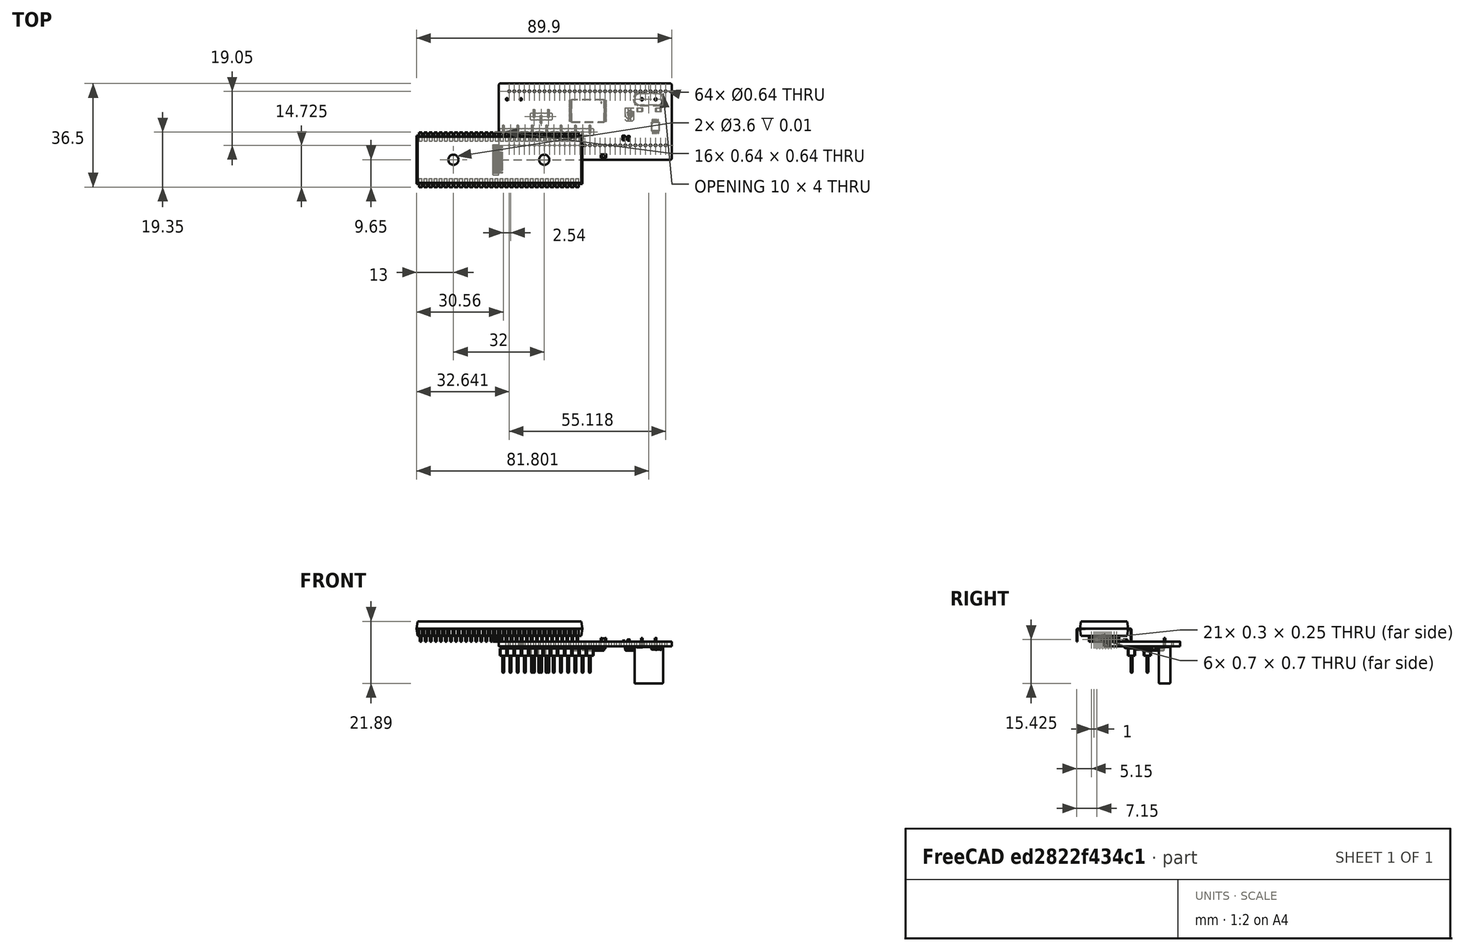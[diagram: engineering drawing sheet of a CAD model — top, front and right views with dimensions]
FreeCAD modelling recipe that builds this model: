
FCSTD DOCUMENT  (FreeCAD 0.19R24291 (Git))
Label: Ultra-MSX-VDP-pinstyle
License: All rights reserved
LicenseURL: http://en.wikipedia.org/wiki/All_rights_reserved
objects: Part::Feature×143, App::Link×51, App::Part×22, PartDesign::CoordinateSystem×1, Sketcher::SketchObject×1
note: 145 computed .brp shape members not serialized (recipe doc carries the construction recipe); baked Part::Feature solids carry a one-line shape summary decoded from their .brp

FEATURE [PartDesign::CoordinateSystem] Local_CS_a649
  AttacherType = Attacher::AttachEngine3D
FEATURE [Part::Feature] Pcb_a649
  Placement = pos=(-95.1,117.3,0) rot=(0,0,1;0rad)
  shape: bbox 60.9 x 26.85 x 1.6 mm, 78 faces (baked)
FEATURE [Sketcher::SketchObject] PCB_Sketch_a649
  FullyConstrained = false
  sketch-geometry (8):
    g0: LineSegment StartX=60.4 StartY=26.85 StartZ=0 EndX=0.5 EndY=26.85 EndZ=0
    g1: LineSegment StartX=4e-16 StartY=26.35 StartZ=0 EndX=1e-16 EndY=0.5 EndZ=0
    g2: LineSegment StartX=0.5 StartY=0 StartZ=0 EndX=60.4 EndY=-1.3e-15 EndZ=0
    g3: LineSegment StartX=60.9 StartY=0.5 StartZ=0 EndX=60.9 EndY=26.35 EndZ=0
    g4: ArcOfCircle CenterX=0.500001 CenterY=26.35 CenterZ=0 NormalX=0 NormalY=0 NormalZ=-1 AngleXU=2.66714e-06 Radius=0.500001 StartAngle=0 EndAngle=1.57079
    g5: ArcOfCircle CenterX=60.4 CenterY=0.500001 CenterZ=0 NormalX=0 NormalY=0 NormalZ=-1 AngleXU=-3.14159 Radius=0.500001 StartAngle=0 EndAngle=1.57079
    g6: ArcOfCircle CenterX=0.500001 CenterY=0.500001 CenterZ=0 NormalX=0 NormalY=0 NormalZ=-1 AngleXU=-1.57079 Radius=0.500001 StartAngle=0 EndAngle=1.57079
    g7: ArcOfCircle CenterX=60.4 CenterY=26.35 CenterZ=0 NormalX=0 NormalY=0 NormalZ=-1 AngleXU=1.5708 Radius=0.500001 StartAngle=0 EndAngle=1.57079
  constraints (8):
    c: Coincident(g1,g6)
    c: Coincident(g1,g4)
    c: Coincident(g2,g6)
    c: Coincident(g0,g4)
    c: Coincident(g2,g5)
    c: Coincident(g0,g7)
    c: Coincident(g3,g5)
    c: Coincident(g3,g7)
FEATURE [Part::Feature] Shape  label="C6_C_0603_1608Metric_e4ffc2d5bdca"
  Placement = pos=(45.7,7.5,0) rot=(0,0,1;1.5708rad)
  shape: bbox 0.8 x 1.6 x 0.8 mm, 28 faces (baked)
FEATURE [Part::Feature] Shape001  label="R82_R_0603_1608Metric_d4caecac030a"
  Placement = pos=(43.95,7.7,0) rot=(0,0,1;1.5708rad)
  shape: bbox 0.8 x 1.6 x 0.45 mm, 26 faces (baked)
FEATURE [App::Link] R82_R_0603_1608Metric_d4caecac030a_ln_  label="R81_R_0603_1608Metric_e3e91bc86c1a"
  LinkPlacement = pos=(47.2,7.9,0) rot=(0,0,1;1.5708rad)
  LinkedObject = -> Shape001
  Placement = pos=(47.2,7.9,0) rot=(0,0,1;1.5708rad)
FEATURE [App::Link] C6_C_0603_1608Metric_e4ffc2d5bdca_ln_  label="C16_C_0603_1608Metric_4bdb616e9b66"
  LinkPlacement = pos=(37.9,3.3,0) rot=(0,0,1;0rad)
  LinkedObject = -> Shape
  Placement = pos=(37.9,3.3,0) rot=(0,0,1;0rad)
FEATURE [App::Link] C6_C_0603_1608Metric_e4ffc2d5bdca_ln_001  label="C8_C_0603_1608Metric_43c608d33d12"
  LinkPlacement = pos=(42.475,7.3,0) rot=(0,0,1;1.5708rad)
  LinkedObject = -> Shape
  Placement = pos=(42.475,7.3,0) rot=(0,0,1;1.5708rad)
FEATURE [Part::Feature] Shape002  label="L3_L_0805_2012Metric_7024b431f41a"
  Placement = pos=(36.8375,1.3,0) rot=(0,0,1;0rad)
  shape: bbox 2 x 1.25 x 1.25 mm, 28 faces (baked)
FEATURE [App::Link] R82_R_0603_1608Metric_d4caecac030a_ln_001  label="R84_R_0603_1608Metric_7d963f7814c4"
  LinkPlacement = pos=(10.7,2.7,0) rot=(0,0,-1;1.5708rad)
  LinkedObject = -> Shape001
  Placement = pos=(10.7,2.7,0) rot=(0,0,-1;1.5708rad)
FEATURE [App::Link] R82_R_0603_1608Metric_d4caecac030a_ln_002  label="R83_R_0603_1608Metric_5f107b2ae899"
  LinkPlacement = pos=(38.475,6.9,0) rot=(0,0,1;3.14159rad)
  LinkedObject = -> Shape001
  Placement = pos=(38.475,6.9,0) rot=(0,0,1;3.14159rad)
FEATURE [App::Link] C6_C_0603_1608Metric_e4ffc2d5bdca_ln_002  label="C14_C_0603_1608Metric_0866816aecf6"
  LinkPlacement = pos=(15.3,25.7,0) rot=(0,0,1;3.14159rad)
  LinkedObject = -> Shape
  Placement = pos=(15.3,25.7,0) rot=(0,0,1;3.14159rad)
FEATURE [App::Link] R82_R_0603_1608Metric_d4caecac030a_ln_003  label="R60_R_0603_1608Metric_ee9b7d5e1906"
  LinkPlacement = pos=(23.9125,3.00625,0) rot=(0,0,1;0rad)
  LinkedObject = -> Shape001
  Placement = pos=(23.9125,3.00625,0) rot=(0,0,1;0rad)
FEATURE [App::Link] C6_C_0603_1608Metric_e4ffc2d5bdca_ln_003  label="C7_C_0603_1608Metric_cf974e6831ff"
  LinkPlacement = pos=(40.75,7.325,0) rot=(0,0,1;1.5708rad)
  LinkedObject = -> Shape
  Placement = pos=(40.75,7.325,0) rot=(0,0,1;1.5708rad)
FEATURE [App::Link] R82_R_0603_1608Metric_d4caecac030a_ln_004  label="R27_R_0603_1608Metric_a411e8e7a906"
  LinkPlacement = pos=(57.3,7.7,-1.6) rot=(0,1,0;3.14159rad)
  LinkedObject = -> Shape001
  Placement = pos=(57.3,7.7,-1.6) rot=(0,1,0;3.14159rad)
FEATURE [App::Link] R82_R_0603_1608Metric_d4caecac030a_ln_005  label="R14_R_0603_1608Metric_b666e58988c9"
  LinkPlacement = pos=(37.9,1.4,-1.6) rot=(0,1,0;3.14159rad)
  LinkedObject = -> Shape001
  Placement = pos=(37.9,1.4,-1.6) rot=(0,1,0;3.14159rad)
FEATURE [App::Link] R82_R_0603_1608Metric_d4caecac030a_ln_006  label="R53_R_0603_1608Metric_dd796e6052a9"
  LinkPlacement = pos=(16.5,7.3,-1.6) rot=(1,0,0;3.14159rad)
  LinkedObject = -> Shape001
  Placement = pos=(16.5,7.3,-1.6) rot=(1,0,0;3.14159rad)
FEATURE [App::Link] C6_C_0603_1608Metric_e4ffc2d5bdca_ln_005  label="C15_C_0603_1608Metric_af0c3dbdae54"
  LinkPlacement = pos=(57.7,11.7,-1.6) rot=(0.707107,-0.707107,0;3.14159rad)
  LinkedObject = -> Shape
  Placement = pos=(57.7,11.7,-1.6) rot=(0.707107,-0.707107,0;3.14159rad)
FEATURE [App::Link] R82_R_0603_1608Metric_d4caecac030a_ln_007  label="R21_R_0603_1608Metric_f35c04f488f9"
  LinkPlacement = pos=(50,8.2125,-1.6) rot=(0.707107,0.707107,0;3.14159rad)
  LinkedObject = -> Shape001
  Placement = pos=(50,8.2125,-1.6) rot=(0.707107,0.707107,0;3.14159rad)
FEATURE [Part::Feature] Shape003  label="R4_R_0805_2012Metric_f107bcb44f6e"
  Placement = pos=(49.5875,17.65,-1.6) rot=(1,0,0;3.14159rad)
  shape: bbox 2 x 1.2 x 0.45 mm, 26 faces (baked)
FEATURE [App::Link] R82_R_0603_1608Metric_d4caecac030a_ln_008  label="R23_R_0603_1608Metric_cfb541b6819d"
  LinkPlacement = pos=(34.4,11.05,-1.6) rot=(0.707107,0.707107,0;3.14159rad)
  LinkedObject = -> Shape001
  Placement = pos=(34.4,11.05,-1.6) rot=(0.707107,0.707107,0;3.14159rad)
FEATURE [App::Link] R82_R_0603_1608Metric_d4caecac030a_ln_009  label="R15_R_0603_1608Metric_62d8d2cdaec6"
  LinkPlacement = pos=(43.9,1.7,-1.6) rot=(0.707107,-0.707107,0;3.14159rad)
  LinkedObject = -> Shape001
  Placement = pos=(43.9,1.7,-1.6) rot=(0.707107,-0.707107,0;3.14159rad)
FEATURE [Part::Feature] Shape004  label="U6_VSSOP_10_3x3mm_P05mm_53867965ed20"
  Placement = pos=(55.15,11.7,-1.6) rot=(0.707107,-0.707107,0;3.14159rad)
  shape: bbox 3 x 4.9 x 1.2 mm, 186 faces (baked)
FEATURE [App::Link] C6_C_0603_1608Metric_e4ffc2d5bdca_ln_006  label="C3_C_0603_1608Metric_be4dabc485b9"
  LinkPlacement = pos=(59.7,21.2,-1.6) rot=(0.707107,0.707107,0;3.14159rad)
  LinkedObject = -> Shape
  Placement = pos=(59.7,21.2,-1.6) rot=(0.707107,0.707107,0;3.14159rad)
FEATURE [App::Link] R82_R_0603_1608Metric_d4caecac030a_ln_010  label="R1_R_0603_1608Metric_ed6f3b55dae2"
  LinkPlacement = pos=(12.8,21.75,-1.6) rot=(0.382683,0.92388,0;3.14159rad)
  LinkedObject = -> Shape001
  Placement = pos=(12.8,21.75,-1.6) rot=(0.382683,0.92388,0;3.14159rad)
FEATURE [App::Link] R82_R_0603_1608Metric_d4caecac030a_ln_011  label="R49_R_0603_1608Metric_953d89943b0f"
  LinkPlacement = pos=(31.9,7.3,-1.6) rot=(1,0,0;3.14159rad)
  LinkedObject = -> Shape001
  Placement = pos=(31.9,7.3,-1.6) rot=(1,0,0;3.14159rad)
FEATURE [Part::Feature] Shape005  label="U14_TSOP_I_28_118x8mm_P055mm_c181658d2376"
  Placement = pos=(31.3,17.25,-1.6) rot=(0,1,0;3.14159rad)
  shape: bbox 13.2 x 8 x 1.6 mm, 456 faces (baked)
FEATURE [Part::Feature] Shape006  label="Y3_Crystal_HC49-U_Vertical_0fe1bbda450f"
  Placement = pos=(55.2409,21.3,-1.6) rot=(0,1,0;3.14159rad)
  shape: bbox 10.9 x 4.65 x 16 mm, 26 faces (baked)
FEATURE [App::Link] R4_R_0805_2012Metric_f107bcb44f6e_ln_  label="R2_R_0805_2012Metric_293fb1e13199"
  LinkPlacement = pos=(6.3,17.6,-1.6) rot=(1,0,0;3.14159rad)
  LinkedObject = -> Shape003
  Placement = pos=(6.3,17.6,-1.6) rot=(1,0,0;3.14159rad)
FEATURE [App::Link] R82_R_0603_1608Metric_d4caecac030a_ln_012  label="R5_R_0603_1608Metric_b329b1c24be4"
  LinkPlacement = pos=(16.8166,21.9834,-1.6) rot=(0.382683,0.92388,0;3.14159rad)
  LinkedObject = -> Shape001
  Placement = pos=(16.8166,21.9834,-1.6) rot=(0.382683,0.92388,0;3.14159rad)
FEATURE [Part::Feature] Shape007  label="C5_Sprague_Goodman_SGC3_37e8c659f2e6"
  Placement = pos=(46.025,15.9,-1.6) rot=(0.707107,0.707107,0;3.14159rad)
  shape: bbox 3.247 x 4.625 x 1.5 mm, 36 faces (baked)
FEATURE [App::Link] R82_R_0603_1608Metric_d4caecac030a_ln_013  label="R61_R_0603_1608Metric_2d9e7edbb70d"
  LinkPlacement = pos=(58.75,9.175,-1.6) rot=(0,1,0;3.14159rad)
  LinkedObject = -> Shape001
  Placement = pos=(58.75,9.175,-1.6) rot=(0,1,0;3.14159rad)
FEATURE [App::Link] R82_R_0603_1608Metric_d4caecac030a_ln_014  label="R7_R_0603_1608Metric_b15c88e18e3f"
  LinkPlacement = pos=(23.1,22.1,-1.6) rot=(1,0,0;3.14159rad)
  LinkedObject = -> Shape001
  Placement = pos=(23.1,22.1,-1.6) rot=(1,0,0;3.14159rad)
FEATURE [App::Link] R82_R_0603_1608Metric_d4caecac030a_ln_015  label="R54_R_0603_1608Metric_722876daf014"
  LinkPlacement = pos=(21.55,7.3,-1.6) rot=(0,1,0;3.14159rad)
  LinkedObject = -> Shape001
  Placement = pos=(21.55,7.3,-1.6) rot=(0,1,0;3.14159rad)
FEATURE [App::Link] R82_R_0603_1608Metric_d4caecac030a_ln_016  label="R6_R_0603_1608Metric_8a82445061e6"
  LinkPlacement = pos=(31.45,22.35,-1.6) rot=(0,1,0;3.14159rad)
  LinkedObject = -> Shape001
  Placement = pos=(31.45,22.35,-1.6) rot=(0,1,0;3.14159rad)
FEATURE [App::Link] C5_Sprague_Goodman_SGC3_37e8c659f2e6_ln_  label="C1_Sprague_Goodman_SGC3_dd31bb1523f4"
  LinkPlacement = pos=(4.5,14.75,-1.6) rot=(1,0,0;3.14159rad)
  LinkedObject = -> Shape007
  Placement = pos=(4.5,14.75,-1.6) rot=(1,0,0;3.14159rad)
FEATURE [App::Link] C6_C_0603_1608Metric_e4ffc2d5bdca_ln_007  label="C2_C_0603_1608Metric_0b1b18837ebd"
  LinkPlacement = pos=(3.1,17.8,-1.6) rot=(1,0,0;3.14159rad)
  LinkedObject = -> Shape
  Placement = pos=(3.1,17.8,-1.6) rot=(1,0,0;3.14159rad)
FEATURE [App::Link] R82_R_0603_1608Metric_d4caecac030a_ln_017  label="R57_R_0603_1608Metric_aec65f8ff485"
  LinkPlacement = pos=(9.5,12.1,-1.6) rot=(0,1,0;3.14159rad)
  LinkedObject = -> Shape001
  Placement = pos=(9.5,12.1,-1.6) rot=(0,1,0;3.14159rad)
FEATURE [Part::Feature] Shape008  label="C73_C_0805_2012Metric_05153e2cdc69"
  Placement = pos=(56.2,17.5,-1.6) rot=(0,1,0;3.14159rad)
  shape: bbox 2 x 1.25 x 1.25 mm, 28 faces (baked)
FEATURE [App::Link] R82_R_0603_1608Metric_d4caecac030a_ln_018  label="R20_R_0603_1608Metric_7d7dade67ea7"
  LinkPlacement = pos=(24.3,12.1,-1.6) rot=(1,0,0;3.14159rad)
  LinkedObject = -> Shape001
  Placement = pos=(24.3,12.1,-1.6) rot=(1,0,0;3.14159rad)
FEATURE [App::Link] R82_R_0603_1608Metric_d4caecac030a_ln_019  label="R13_R_0603_1608Metric_307ab71b2f2b"
  LinkPlacement = pos=(41.65,1.65,-1.6) rot=(0,1,0;3.14159rad)
  LinkedObject = -> Shape001
  Placement = pos=(41.65,1.65,-1.6) rot=(0,1,0;3.14159rad)
FEATURE [App::Link] R82_R_0603_1608Metric_d4caecac030a_ln_020  label="R51_R_0603_1608Metric_7bd6d0df39b7"
  LinkPlacement = pos=(19.5,12.1,-1.6) rot=(1,0,0;3.14159rad)
  LinkedObject = -> Shape001
  Placement = pos=(19.5,12.1,-1.6) rot=(1,0,0;3.14159rad)
FEATURE [App::Link] R82_R_0603_1608Metric_d4caecac030a_ln_021  label="R22_R_0603_1608Metric_cb1c37444e2f"
  LinkPlacement = pos=(52.6,8.2125,-1.6) rot=(0.707107,0.707107,0;3.14159rad)
  LinkedObject = -> Shape001
  Placement = pos=(52.6,8.2125,-1.6) rot=(0.707107,0.707107,0;3.14159rad)
FEATURE [App::Link] C6_C_0603_1608Metric_e4ffc2d5bdca_ln_008  label="C12_C_0603_1608Metric_32ee04979fd2"
  LinkPlacement = pos=(52.55,11.925,-1.6) rot=(0.707107,0.707107,0;3.14159rad)
  LinkedObject = -> Shape
  Placement = pos=(52.55,11.925,-1.6) rot=(0.707107,0.707107,0;3.14159rad)
FEATURE [App::Link] C6_C_0603_1608Metric_e4ffc2d5bdca_ln_009  label="C10_C_0603_1608Metric_ed01532d6a4e"
  LinkPlacement = pos=(38.1,2.9,-1.6) rot=(1,0,0;3.14159rad)
  LinkedObject = -> Shape
  Placement = pos=(38.1,2.9,-1.6) rot=(1,0,0;3.14159rad)
FEATURE [App::Link] R82_R_0603_1608Metric_d4caecac030a_ln_022  label="R56_R_0603_1608Metric_1c0ae7ad8c6e"
  LinkPlacement = pos=(1.9,7.3,-1.6) rot=(0,1,0;3.14159rad)
  LinkedObject = -> Shape001
  Placement = pos=(1.9,7.3,-1.6) rot=(0,1,0;3.14159rad)
FEATURE [App::Link] R82_R_0603_1608Metric_d4caecac030a_ln_023  label="R50_R_0603_1608Metric_f5e2b95ccbbe"
  LinkPlacement = pos=(29.7,12.05,-1.6) rot=(0,1,0;3.14159rad)
  LinkedObject = -> Shape001
  Placement = pos=(29.7,12.05,-1.6) rot=(0,1,0;3.14159rad)
FEATURE [App::Link] C6_C_0603_1608Metric_e4ffc2d5bdca_ln_010  label="C17_C_0603_1608Metric_ba9556bdb5b0"
  LinkPlacement = pos=(54.95,15.7,-1.6) rot=(0,1,0;3.14159rad)
  LinkedObject = -> Shape
  Placement = pos=(54.95,15.7,-1.6) rot=(0,1,0;3.14159rad)
FEATURE [App::Link] R82_R_0603_1608Metric_d4caecac030a_ln_024  label="R25_R_0603_1608Metric_d3d0e9069176"
  LinkPlacement = pos=(34.35,7.95,-1.6) rot=(0.707107,0.707107,0;3.14159rad)
  LinkedObject = -> Shape001
  Placement = pos=(34.35,7.95,-1.6) rot=(0.707107,0.707107,0;3.14159rad)
FEATURE [App::Link] C6_C_0603_1608Metric_e4ffc2d5bdca_ln_011  label="C18_C_0603_1608Metric_0a9993050c82"
  LinkPlacement = pos=(57.7,14.9,-1.6) rot=(0.707107,-0.707107,0;3.14159rad)
  LinkedObject = -> Shape
  Placement = pos=(57.7,14.9,-1.6) rot=(0.707107,-0.707107,0;3.14159rad)
FEATURE [App::Link] R82_R_0603_1608Metric_d4caecac030a_ln_025  label="R52_R_0603_1608Metric_1314e578b8fa"
  LinkPlacement = pos=(26.9875,7.3,-1.6) rot=(1,0,0;3.14159rad)
  LinkedObject = -> Shape001
  Placement = pos=(26.9875,7.3,-1.6) rot=(1,0,0;3.14159rad)
FEATURE [App::Link] R82_R_0603_1608Metric_d4caecac030a_ln_026  label="R59_R_0603_1608Metric_51d35e5e8522"
  LinkPlacement = pos=(11.45,7.3,-1.6) rot=(1,0,0;3.14159rad)
  LinkedObject = -> Shape001
  Placement = pos=(11.45,7.3,-1.6) rot=(1,0,0;3.14159rad)
FEATURE [App::Link] Y3_Crystal_HC49_U_Vertical_0fe1bbda450f_ln_  label="Y1_Crystal_HC49-U_Vertical_8a092cbe764f"
  LinkPlacement = pos=(2.85906,21.3,-1.6) rot=(1,0,0;3.14159rad)
  LinkedObject = -> Shape006
  Placement = pos=(2.85906,21.3,-1.6) rot=(1,0,0;3.14159rad)
FEATURE [App::Link] R82_R_0603_1608Metric_d4caecac030a_ln_027  label="R9_R_0603_1608Metric_e8e6f4d4817b"
  LinkPlacement = pos=(52.55,14.9,-1.6) rot=(0.707107,-0.707107,0;3.14159rad)
  LinkedObject = -> Shape001
  Placement = pos=(52.55,14.9,-1.6) rot=(0.707107,-0.707107,0;3.14159rad)
FEATURE [Part::Feature] Shape009  label="J3_PinHeader_1x13_P254mm_Vertical_SMD_Pin1Left_9baea8a7431d"
  Placement = pos=(16.8,9.7,-1.6) rot=(0.707107,-0.707107,0;3.14159rad)
  shape: bbox 33.02 x 5 x 9.3 mm, 355 faces (baked)
FEATURE [App::Link] C6_C_0603_1608Metric_e4ffc2d5bdca_ln_012  label="C13_C_0603_1608Metric_7b6bf5430122"
  LinkPlacement = pos=(20.675,16.7,-1.6) rot=(0,1,0;3.14159rad)
  LinkedObject = -> Shape
  Placement = pos=(20.675,16.7,-1.6) rot=(0,1,0;3.14159rad)
FEATURE [App::Link] R82_R_0603_1608Metric_d4caecac030a_ln_028  label="R8_R_0603_1608Metric_03eb6692b740"
  LinkPlacement = pos=(22.3,13.7,-1.6) rot=(0,1,0;3.14159rad)
  LinkedObject = -> Shape001
  Placement = pos=(22.3,13.7,-1.6) rot=(0,1,0;3.14159rad)
FEATURE [Part::Feature] Shape010  label="JP5_PinHeader_1x03_P254mm_Vertical_SMD_Pin1Left_52619bf62036"
  Placement = pos=(14.9,15.25,-1.6) rot=(0.707107,-0.707107,0;3.14159rad)
  shape: bbox 7.62 x 5 x 9.3 mm, 85 faces (baked)
FEATURE [App::Link] C6_C_0603_1608Metric_e4ffc2d5bdca_ln_013  label="C9_C_0603_1608Metric_9afa2d7164e9"
  LinkPlacement = pos=(41.5,3.15,-1.6) rot=(1,0,0;3.14159rad)
  LinkedObject = -> Shape
  Placement = pos=(41.5,3.15,-1.6) rot=(1,0,0;3.14159rad)
FEATURE [App::Link] C6_C_0603_1608Metric_e4ffc2d5bdca_ln_014  label="C4_C_0603_1608Metric_4d1428f5722c"
  LinkPlacement = pos=(52.75,17.8,-1.6) rot=(0,1,0;3.14159rad)
  LinkedObject = -> Shape
  Placement = pos=(52.75,17.8,-1.6) rot=(0,1,0;3.14159rad)
FEATURE [App::Link] R82_R_0603_1608Metric_d4caecac030a_ln_029  label="R3_R_0603_1608Metric_36257eaa7fe0"
  LinkPlacement = pos=(45.4,19.3,-1.6) rot=(0,1,0;3.14159rad)
  LinkedObject = -> Shape001
  Placement = pos=(45.4,19.3,-1.6) rot=(0,1,0;3.14159rad)
FEATURE [App::Link] R82_R_0603_1608Metric_d4caecac030a_ln_030  label="R58_R_0603_1608Metric_b9a300878665"
  LinkPlacement = pos=(14.7,22,-1.6) rot=(0.92388,-0.382683,0;3.14159rad)
  LinkedObject = -> Shape001
  Placement = pos=(14.7,22,-1.6) rot=(0.92388,-0.382683,0;3.14159rad)
FEATURE [App::Link] R82_R_0603_1608Metric_d4caecac030a_ln_031  label="R55_R_0603_1608Metric_c16f27e9f752"
  LinkPlacement = pos=(6.7,7.3,-1.6) rot=(1,0,0;3.14159rad)
  LinkedObject = -> Shape001
  Placement = pos=(6.7,7.3,-1.6) rot=(1,0,0;3.14159rad)
FEATURE [App::Link] R82_R_0603_1608Metric_d4caecac030a_ln_032  label="R11_R_0603_1608Metric_86f9d7e7f3b2"
  LinkPlacement = pos=(20.725,15.2,-1.6) rot=(0,1,0;3.14159rad)
  LinkedObject = -> Shape001
  Placement = pos=(20.725,15.2,-1.6) rot=(0,1,0;3.14159rad)
FEATURE [App::Part] Bot_a649
  Group = -> [R82_R_0603_1608Metric_d4caecac030a_ln_004,R82_R_0603_1608Metric_d4caecac030a_ln_005,R82_R_0603_1608Metric_d4caecac030a_ln_006,C6_C_0603_1608Metric_e4ffc2d5bdca_ln_005,R82_R_0603_1608Metric_d4caecac030a_ln_007,Shape003,R82_R_0603_1608Metric_d4caecac030a_ln_008,R82_R_0603_1608Metric_d4caecac030a_ln_009,Shape004,C6_C_0603_1608Metric_e4ffc2d5bdca_ln_006,R82_R_0603_1608Metric_d4caecac030a_ln_010,+39 more]
  Origin = -> Origin004
FEATURE [Part::Feature] Part__Feature  label="Chamfer007"
  Placement = pos=(-16,0,7.18) rot=(0,0,1;0rad)
  shape: bbox 58.4 x 17 x 5.19 mm, 18 faces (baked)
FEATURE [Part::Feature] Part__Feature001  label="Pins"
  shape: bbox 1.025 x 3.05 x 4.6 mm, 14 faces (baked)
FEATURE [Part::Feature] Part__Feature002  label="Pins001"
  shape: bbox 1.025 x 3.05 x 4.6 mm, 14 faces (baked)
FEATURE [Part::Feature] Part__Feature003  label="Pins002"
  shape: bbox 1.025 x 3.05 x 4.6 mm, 14 faces (baked)
FEATURE [Part::Feature] Part__Feature004  label="Pins003"
  shape: bbox 1.025 x 3.05 x 4.6 mm, 14 faces (baked)
FEATURE [Part::Feature] Part__Feature005  label="Pins004"
  shape: bbox 1.025 x 3.05 x 4.6 mm, 14 faces (baked)
FEATURE [Part::Feature] Part__Feature006  label="Pins005"
  shape: bbox 1.025 x 3.05 x 4.6 mm, 14 faces (baked)
FEATURE [Part::Feature] Part__Feature007  label="Pins006"
  shape: bbox 1.025 x 3.05 x 4.6 mm, 14 faces (baked)
FEATURE [Part::Feature] Part__Feature008  label="Pins007"
  shape: bbox 1.025 x 3.05 x 4.6 mm, 14 faces (baked)
FEATURE [Part::Feature] Part__Feature009  label="Pins008"
  shape: bbox 1.025 x 3.05 x 4.6 mm, 14 faces (baked)
FEATURE [Part::Feature] Part__Feature010  label="Pins009"
  shape: bbox 1.025 x 3.05 x 4.6 mm, 14 faces (baked)
FEATURE [Part::Feature] Part__Feature011  label="Pins010"
  shape: bbox 1.025 x 3.05 x 4.6 mm, 14 faces (baked)
FEATURE [Part::Feature] Part__Feature012  label="Pins011"
  shape: bbox 1.025 x 3.05 x 4.6 mm, 14 faces (baked)
FEATURE [Part::Feature] Part__Feature013  label="Pins012"
  shape: bbox 1.025 x 3.05 x 4.6 mm, 14 faces (baked)
FEATURE [Part::Feature] Part__Feature014  label="Pins013"
  shape: bbox 1.025 x 3.05 x 4.6 mm, 14 faces (baked)
FEATURE [Part::Feature] Part__Feature015  label="Pins014"
  shape: bbox 1.025 x 3.05 x 4.6 mm, 14 faces (baked)
FEATURE [Part::Feature] Part__Feature016  label="Pins015"
  shape: bbox 1.025 x 3.05 x 4.6 mm, 14 faces (baked)
FEATURE [Part::Feature] Part__Feature017  label="Pins016"
  shape: bbox 1.025 x 3.05 x 4.6 mm, 14 faces (baked)
FEATURE [Part::Feature] Part__Feature018  label="Pins017"
  shape: bbox 1.025 x 3.05 x 4.6 mm, 14 faces (baked)
FEATURE [Part::Feature] Part__Feature019  label="Pins018"
  shape: bbox 1.025 x 3.05 x 4.6 mm, 14 faces (baked)
FEATURE [Part::Feature] Part__Feature020  label="Pins019"
  shape: bbox 1.025 x 3.05 x 4.6 mm, 14 faces (baked)
FEATURE [Part::Feature] Part__Feature021  label="Pins020"
  shape: bbox 1.025 x 3.05 x 4.6 mm, 14 faces (baked)
FEATURE [Part::Feature] Part__Feature022  label="Pins021"
  shape: bbox 1.025 x 3.05 x 4.6 mm, 14 faces (baked)
FEATURE [Part::Feature] Part__Feature023  label="Pins022"
  shape: bbox 1.025 x 3.05 x 4.6 mm, 14 faces (baked)
FEATURE [Part::Feature] Part__Feature024  label="Pins023"
  shape: bbox 1.025 x 3.05 x 4.6 mm, 14 faces (baked)
FEATURE [Part::Feature] Part__Feature025  label="Pins024"
  shape: bbox 1.025 x 3.05 x 4.6 mm, 14 faces (baked)
FEATURE [Part::Feature] Part__Feature026  label="Pins025"
  shape: bbox 1.025 x 3.05 x 4.6 mm, 14 faces (baked)
FEATURE [Part::Feature] Part__Feature027  label="Pins026"
  shape: bbox 1.025 x 3.05 x 4.6 mm, 14 faces (baked)
FEATURE [Part::Feature] Part__Feature028  label="Pins027"
  shape: bbox 1.025 x 3.05 x 4.6 mm, 14 faces (baked)
FEATURE [Part::Feature] Part__Feature029  label="Pins028"
  shape: bbox 1.025 x 3.05 x 4.6 mm, 14 faces (baked)
FEATURE [Part::Feature] Part__Feature030  label="Pins029"
  shape: bbox 1.025 x 3.05 x 4.6 mm, 14 faces (baked)
FEATURE [Part::Feature] Part__Feature031  label="Pins030"
  shape: bbox 1.025 x 3.05 x 4.6 mm, 14 faces (baked)
FEATURE [Part::Feature] Part__Feature032  label="Pins031"
  shape: bbox 1.025 x 3.05 x 4.6 mm, 14 faces (baked)
FEATURE [App::Part] Pins  label="Pins032"
  Group = -> [Part__Feature001,Part__Feature002,Part__Feature003,Part__Feature004,Part__Feature005,Part__Feature006,Part__Feature007,Part__Feature008,Part__Feature009,Part__Feature010,Part__Feature011,Part__Feature012,Part__Feature013,Part__Feature014,Part__Feature015,Part__Feature016,Part__Feature017,Part__Feature018,Part__Feature019,Part__Feature020,Part__Feature021,Part__Feature022,Part__Feature023,+9 more]
  Origin = -> Origin005
FEATURE [Part::Feature] Part__Feature033  label="Compound"
  shape: bbox 1.025 x 3.05 x 4.6 mm, 14 faces (baked)
FEATURE [Part::Feature] Part__Feature034  label="Compound001"
  shape: bbox 1.025 x 3.05 x 4.6 mm, 14 faces (baked)
FEATURE [Part::Feature] Part__Feature035  label="Compound002"
  shape: bbox 1.025 x 3.05 x 4.6 mm, 14 faces (baked)
FEATURE [Part::Feature] Part__Feature036  label="Compound003"
  shape: bbox 1.025 x 3.05 x 4.6 mm, 14 faces (baked)
FEATURE [Part::Feature] Part__Feature037  label="Compound004"
  shape: bbox 1.025 x 3.05 x 4.6 mm, 14 faces (baked)
FEATURE [Part::Feature] Part__Feature038  label="Compound005"
  shape: bbox 1.025 x 3.05 x 4.6 mm, 14 faces (baked)
FEATURE [Part::Feature] Part__Feature039  label="Compound006"
  shape: bbox 1.025 x 3.05 x 4.6 mm, 14 faces (baked)
FEATURE [Part::Feature] Part__Feature040  label="Compound007"
  shape: bbox 1.025 x 3.05 x 4.6 mm, 14 faces (baked)
FEATURE [Part::Feature] Part__Feature041  label="Compound008"
  shape: bbox 1.025 x 3.05 x 4.6 mm, 14 faces (baked)
FEATURE [Part::Feature] Part__Feature042  label="Compound009"
  shape: bbox 1.025 x 3.05 x 4.6 mm, 14 faces (baked)
FEATURE [Part::Feature] Part__Feature043  label="Compound010"
  shape: bbox 1.025 x 3.05 x 4.6 mm, 14 faces (baked)
FEATURE [Part::Feature] Part__Feature044  label="Compound011"
  shape: bbox 1.025 x 3.05 x 4.6 mm, 14 faces (baked)
FEATURE [Part::Feature] Part__Feature045  label="Compound012"
  shape: bbox 1.025 x 3.05 x 4.6 mm, 14 faces (baked)
FEATURE [Part::Feature] Part__Feature046  label="Compound013"
  shape: bbox 1.025 x 3.05 x 4.6 mm, 14 faces (baked)
FEATURE [Part::Feature] Part__Feature047  label="Compound014"
  shape: bbox 1.025 x 3.05 x 4.6 mm, 14 faces (baked)
FEATURE [Part::Feature] Part__Feature048  label="Compound015"
  shape: bbox 1.025 x 3.05 x 4.6 mm, 14 faces (baked)
FEATURE [Part::Feature] Part__Feature049  label="Compound016"
  shape: bbox 1.025 x 3.05 x 4.6 mm, 14 faces (baked)
FEATURE [Part::Feature] Part__Feature050  label="Compound017"
  shape: bbox 1.025 x 3.05 x 4.6 mm, 14 faces (baked)
FEATURE [Part::Feature] Part__Feature051  label="Compound018"
  shape: bbox 1.025 x 3.05 x 4.6 mm, 14 faces (baked)
FEATURE [Part::Feature] Part__Feature052  label="Compound019"
  shape: bbox 1.025 x 3.05 x 4.6 mm, 14 faces (baked)
FEATURE [Part::Feature] Part__Feature053  label="Compound020"
  shape: bbox 1.025 x 3.05 x 4.6 mm, 14 faces (baked)
FEATURE [Part::Feature] Part__Feature054  label="Compound021"
  shape: bbox 1.025 x 3.05 x 4.6 mm, 14 faces (baked)
FEATURE [Part::Feature] Part__Feature055  label="Compound022"
  shape: bbox 1.025 x 3.05 x 4.6 mm, 14 faces (baked)
FEATURE [Part::Feature] Part__Feature056  label="Compound023"
  shape: bbox 1.025 x 3.05 x 4.6 mm, 14 faces (baked)
FEATURE [Part::Feature] Part__Feature057  label="Compound024"
  shape: bbox 1.025 x 3.05 x 4.6 mm, 14 faces (baked)
FEATURE [Part::Feature] Part__Feature058  label="Compound025"
  shape: bbox 1.025 x 3.05 x 4.6 mm, 14 faces (baked)
FEATURE [Part::Feature] Part__Feature059  label="Compound026"
  shape: bbox 1.025 x 3.05 x 4.6 mm, 14 faces (baked)
FEATURE [Part::Feature] Part__Feature060  label="Compound027"
  shape: bbox 1.025 x 3.05 x 4.6 mm, 14 faces (baked)
FEATURE [Part::Feature] Part__Feature061  label="Compound028"
  shape: bbox 1.025 x 3.05 x 4.6 mm, 14 faces (baked)
FEATURE [Part::Feature] Part__Feature062  label="Compound029"
  shape: bbox 1.025 x 3.05 x 4.6 mm, 14 faces (baked)
FEATURE [Part::Feature] Part__Feature063  label="Compound030"
  shape: bbox 1.025 x 3.05 x 4.6 mm, 14 faces (baked)
FEATURE [Part::Feature] Part__Feature064  label="Compound031"
  shape: bbox 1.025 x 3.05 x 4.6 mm, 14 faces (baked)
FEATURE [App::Part] Compound  label="Compound032"
  Group = -> [Part__Feature033,Part__Feature034,Part__Feature035,Part__Feature036,Part__Feature037,Part__Feature038,Part__Feature039,Part__Feature040,Part__Feature041,Part__Feature042,Part__Feature043,Part__Feature044,Part__Feature045,Part__Feature046,Part__Feature047,Part__Feature048,Part__Feature049,Part__Feature050,Part__Feature051,Part__Feature052,Part__Feature053,Part__Feature054,Part__Feature055,+9 more]
  Origin = -> Origin006
FEATURE [App::Part] DIL_64
  Group = -> [Part__Feature,Pins,Compound]
  Origin = -> Origin007
  Placement = pos=(31.18,14.55,-0.5) rot=(0,0,1;0rad)
FEATURE [Part::Feature] pads_area018001  label="topPads_a649"
  Placement = pos=(-95.1,117.3,0.02) rot=(0,0,1;0rad)
  shape: bbox 59.9 x 26.25 x 2e-07 mm, 287 faces, 0 solids (baked)
FEATURE [Part::Feature] pads_area018057001  label="botPads_a649"
  Placement = pos=(-95.1,117.3,-1.62) rot=(0,0,1;0rad)
  shape: bbox 59.9 x 26.25 x 2e-07 mm, 429 faces, 0 solids (baked)
FEATURE [App::Part] Board_Geoms_a649
  Group = -> [Local_CS_a649,Pcb_a649,PCB_Sketch_a649,pads_area018001,pads_area018057001]
  Origin = -> Origin
FEATURE [Part::Feature] Part__Feature065  label="Leg1"
  shape: bbox 3.3 x 0.5 x 0.975 mm, 29 faces (baked)
FEATURE [Part::Feature] Part__Feature066  label="Leg002"
  Placement = pos=(0,-1,0) rot=(0,0,1;0rad)
  shape: bbox 3.3 x 0.5 x 0.975 mm, 29 faces (baked)
FEATURE [Part::Feature] Part__Feature067  label="Leg003"
  Placement = pos=(0,-2,0) rot=(0,0,1;0rad)
  shape: bbox 3.3 x 0.5 x 0.975 mm, 29 faces (baked)
FEATURE [Part::Feature] Part__Feature068  label="Leg004"
  Placement = pos=(0,-3,0) rot=(0,0,1;0rad)
  shape: bbox 3.3 x 0.5 x 0.975 mm, 29 faces (baked)
FEATURE [Part::Feature] Part__Feature069  label="Leg005"
  Placement = pos=(0,-4,0) rot=(0,0,1;0rad)
  shape: bbox 3.3 x 0.5 x 0.975 mm, 29 faces (baked)
FEATURE [App::Part] Legs
  Group = -> [Part__Feature065,Part__Feature066,Part__Feature067,Part__Feature068,Part__Feature069]
  Origin = -> Origin008
  Placement = pos=(0,-2.5,0) rot=(0,0,1;0rad)
FEATURE [Part::Feature] Part__Feature070  label="Plastic_casing"
  Placement = pos=(0,-2.5,0) rot=(0,0,1;0rad)
  shape: bbox 2.1 x 5.75 x 1.5 mm, 46 faces (baked)
FEATURE [App::Part] Unnamed  label="BCT05"
  Group = -> [Legs,Part__Feature070]
  Origin = -> Origin009
  Placement = pos=(42.1,2,0) rot=(0,0,1;1.5708rad)
FEATURE [Part::Feature] Part__Feature071  label="Leg006"
  Placement = pos=(0,-4,0) rot=(0,0,1;0rad)
  shape: bbox 3.3 x 0.5 x 0.975 mm, 29 faces (baked)
FEATURE [Part::Feature] Part__Feature072  label="Plastic_casing001"
  Placement = pos=(0,-2.5,0) rot=(0,0,1;0rad)
  shape: bbox 2.1 x 5.75 x 1.5 mm, 46 faces (baked)
FEATURE [Part::Feature] Part__Feature073  label="Leg007"
  Placement = pos=(0,-1,0) rot=(0,0,1;0rad)
  shape: bbox 3.3 x 0.5 x 0.975 mm, 29 faces (baked)
FEATURE [Part::Feature] Part__Feature074  label="Leg008"
  Placement = pos=(0,-3,0) rot=(0,0,1;0rad)
  shape: bbox 3.3 x 0.5 x 0.975 mm, 29 faces (baked)
FEATURE [Part::Feature] Part__Feature075  label="Leg009"
  Placement = pos=(0,-2,0) rot=(0,0,1;0rad)
  shape: bbox 3.3 x 0.5 x 0.975 mm, 29 faces (baked)
FEATURE [Part::Feature] Part__Feature076  label="Leg010"
  shape: bbox 3.3 x 0.5 x 0.975 mm, 29 faces (baked)
FEATURE [App::Part] Legs001
  Group = -> [Part__Feature076,Part__Feature073,Part__Feature075,Part__Feature074,Part__Feature071]
  Origin = -> Origin011
  Placement = pos=(0,-2.5,0) rot=(0,0,1;0rad)
FEATURE [App::Part] Unnamed001  label="BCT05-2"
  Group = -> [Legs001,Part__Feature072]
  Origin = -> Origin010
  Placement = pos=(57.3,2,0) rot=(0,0,1;1.5708rad)
FEATURE [Part::Feature] Part__Feature077  label="Chamfer"
  Placement = pos=(-3,-2.75,0.475) rot=(0,0,1;0rad)
  shape: bbox 2.1 x 6.75 x 1.5 mm, 54 faces (baked)
FEATURE [Part::Feature] Part__Feature078  label="Leg011"
  Placement = pos=(0,-3.5,0) rot=(0,0,1;0rad)
  shape: bbox 3.3 x 0.5 x 0.975 mm, 29 faces (baked)
FEATURE [Part::Feature] Part__Feature079  label="Leg012"
  Placement = pos=(0,-7.5,0) rot=(0,0,1;0rad)
  shape: bbox 3.3 x 0.5 x 0.975 mm, 29 faces (baked)
FEATURE [Part::Feature] Part__Feature080  label="Leg013"
  Placement = pos=(0,-5.5,0) rot=(0,0,1;0rad)
  shape: bbox 3.3 x 0.5 x 0.975 mm, 29 faces (baked)
FEATURE [Part::Feature] Part__Feature081  label="Leg014"
  Placement = pos=(0,-4.5,0) rot=(0,0,1;0rad)
  shape: bbox 3.3 x 0.5 x 0.975 mm, 29 faces (baked)
FEATURE [Part::Feature] Part__Feature082  label="Leg015"
  Placement = pos=(0,-6.5,0) rot=(0,0,1;0rad)
  shape: bbox 3.3 x 0.5 x 0.975 mm, 29 faces (baked)
FEATURE [Part::Feature] Part__Feature083  label="Leg016"
  Placement = pos=(0,-2.5,0) rot=(0,0,1;0rad)
  shape: bbox 3.3 x 0.5 x 0.975 mm, 29 faces (baked)
FEATURE [App::Part] Legs002
  Group = -> [Part__Feature083,Part__Feature078,Part__Feature081,Part__Feature080,Part__Feature082,Part__Feature079]
  Origin = -> Origin012
  Placement = pos=(0,0.5,0) rot=(0,0,1;0rad)
FEATURE [App::Part] GCT_BC075_06
  Group = -> [Legs002,Part__Feature077]
  Origin = -> Origin013
  Placement = pos=(18.1,2,0) rot=(0,0,1;1.5708rad)
FEATURE [Part::Feature] Part__Feature084  label="Chamfer008"
  Placement = pos=(-3,-4.75,0.475) rot=(0,0,1;0rad)
  shape: bbox 2.1 x 10.75 x 1.5 mm, 86 faces (baked)
FEATURE [Part::Feature] Part__Feature085  label="Leg017"
  shape: bbox 3.3 x 0.5 x 0.975 mm, 28 faces (baked)
FEATURE [Part::Feature] Part__Feature086  label="Leg018"
  Placement = pos=(0,-1,0) rot=(0,0,1;0rad)
  shape: bbox 3.3 x 0.5 x 0.975 mm, 28 faces (baked)
FEATURE [Part::Feature] Part__Feature087  label="Leg019"
  Placement = pos=(0,-2,0) rot=(0,0,1;0rad)
  shape: bbox 3.3 x 0.5 x 0.975 mm, 28 faces (baked)
FEATURE [Part::Feature] Part__Feature088  label="Leg020"
  Placement = pos=(0,-3,0) rot=(0,0,1;0rad)
  shape: bbox 3.3 x 0.5 x 0.975 mm, 28 faces (baked)
FEATURE [Part::Feature] Part__Feature089  label="Leg021"
  Placement = pos=(0,-4,0) rot=(0,0,1;0rad)
  shape: bbox 3.3 x 0.5 x 0.975 mm, 28 faces (baked)
FEATURE [Part::Feature] Part__Feature090  label="Leg022"
  Placement = pos=(0,-5,0) rot=(0,0,1;0rad)
  shape: bbox 3.3 x 0.5 x 0.975 mm, 28 faces (baked)
FEATURE [Part::Feature] Part__Feature091  label="Leg023"
  Placement = pos=(0,-6,0) rot=(0,0,1;0rad)
  shape: bbox 3.3 x 0.5 x 0.975 mm, 28 faces (baked)
FEATURE [Part::Feature] Part__Feature092  label="Leg024"
  Placement = pos=(0,-7,0) rot=(0,0,1;0rad)
  shape: bbox 3.3 x 0.5 x 0.975 mm, 28 faces (baked)
FEATURE [Part::Feature] Part__Feature093  label="Leg025"
  Placement = pos=(0,-8,0) rot=(0,0,1;0rad)
  shape: bbox 3.3 x 0.5 x 0.975 mm, 28 faces (baked)
FEATURE [Part::Feature] Part__Feature094  label="Leg026"
  Placement = pos=(0,-9,0) rot=(0,0,1;0rad)
  shape: bbox 3.3 x 0.5 x 0.975 mm, 28 faces (baked)
FEATURE [App::Part] Legs003
  Group = -> [Part__Feature085,Part__Feature086,Part__Feature087,Part__Feature088,Part__Feature089,Part__Feature090,Part__Feature091,Part__Feature092,Part__Feature093,Part__Feature094]
  Origin = -> Origin014
FEATURE [App::Part] GCT_BC075_10
  Group = -> [Part__Feature084,Legs003]
  Origin = -> Origin015
  Placement = pos=(6.5,2,-1.6) rot=(0.707107,0.707107,0;3.14159rad)
FEATURE [Part::Feature] Part__Feature095  label="Chamfer009"
  Placement = pos=(-3,-4.75,0.475) rot=(0,0,1;0rad)
  shape: bbox 2.1 x 10.75 x 1.5 mm, 86 faces (baked)
FEATURE [Part::Feature] Part__Feature096  label="Leg027"
  Placement = pos=(0,-2,0) rot=(0,0,1;0rad)
  shape: bbox 3.3 x 0.5 x 0.975 mm, 28 faces (baked)
FEATURE [Part::Feature] Part__Feature097  label="Leg028"
  Placement = pos=(0,-3,0) rot=(0,0,1;0rad)
  shape: bbox 3.3 x 0.5 x 0.975 mm, 28 faces (baked)
FEATURE [Part::Feature] Part__Feature098  label="Leg029"
  Placement = pos=(0,-1,0) rot=(0,0,1;0rad)
  shape: bbox 3.3 x 0.5 x 0.975 mm, 28 faces (baked)
FEATURE [Part::Feature] Part__Feature099  label="Leg030"
  shape: bbox 3.3 x 0.5 x 0.975 mm, 28 faces (baked)
FEATURE [Part::Feature] Part__Feature100  label="Leg031"
  Placement = pos=(0,-4,0) rot=(0,0,1;0rad)
  shape: bbox 3.3 x 0.5 x 0.975 mm, 28 faces (baked)
FEATURE [Part::Feature] Part__Feature101  label="Leg032"
  Placement = pos=(0,-8,0) rot=(0,0,1;0rad)
  shape: bbox 3.3 x 0.5 x 0.975 mm, 28 faces (baked)
FEATURE [Part::Feature] Part__Feature102  label="Leg033"
  Placement = pos=(0,-5,0) rot=(0,0,1;0rad)
  shape: bbox 3.3 x 0.5 x 0.975 mm, 28 faces (baked)
FEATURE [Part::Feature] Part__Feature103  label="Leg034"
  Placement = pos=(0,-9,0) rot=(0,0,1;0rad)
  shape: bbox 3.3 x 0.5 x 0.975 mm, 28 faces (baked)
FEATURE [Part::Feature] Part__Feature104  label="Leg035"
  Placement = pos=(0,-6,0) rot=(0,0,1;0rad)
  shape: bbox 3.3 x 0.5 x 0.975 mm, 28 faces (baked)
FEATURE [Part::Feature] Part__Feature105  label="Leg036"
  Placement = pos=(0,-7,0) rot=(0,0,1;0rad)
  shape: bbox 3.3 x 0.5 x 0.975 mm, 28 faces (baked)
FEATURE [App::Part] Legs004
  Group = -> [Part__Feature099,Part__Feature098,Part__Feature096,Part__Feature097,Part__Feature100,Part__Feature102,Part__Feature104,Part__Feature105,Part__Feature101,Part__Feature103]
  Origin = -> Origin017
FEATURE [App::Part] GCT_BC075_011  label="GCT_BC075_010-2"
  Group = -> [Part__Feature095,Legs004]
  Origin = -> Origin016
  Placement = pos=(18.1,2,-1.6) rot=(0.707107,0.707107,0;3.14159rad)
FEATURE [Part::Feature] Part__Feature106  label="Leg037"
  Placement = pos=(0,-7,0) rot=(0,0,1;0rad)
  shape: bbox 3.3 x 0.5 x 0.975 mm, 28 faces (baked)
FEATURE [Part::Feature] Part__Feature107  label="Chamfer010"
  Placement = pos=(-3,-4.75,0.475) rot=(0,0,1;0rad)
  shape: bbox 2.1 x 10.75 x 1.5 mm, 86 faces (baked)
FEATURE [Part::Feature] Part__Feature108  label="Leg038"
  Placement = pos=(0,-3,0) rot=(0,0,1;0rad)
  shape: bbox 3.3 x 0.5 x 0.975 mm, 28 faces (baked)
FEATURE [Part::Feature] Part__Feature109  label="Leg039"
  Placement = pos=(0,-2,0) rot=(0,0,1;0rad)
  shape: bbox 3.3 x 0.5 x 0.975 mm, 28 faces (baked)
FEATURE [Part::Feature] Part__Feature110  label="Leg040"
  Placement = pos=(0,-1,0) rot=(0,0,1;0rad)
  shape: bbox 3.3 x 0.5 x 0.975 mm, 28 faces (baked)
FEATURE [Part::Feature] Part__Feature111  label="Leg041"
  shape: bbox 3.3 x 0.5 x 0.975 mm, 28 faces (baked)
FEATURE [Part::Feature] Part__Feature112  label="Leg042"
  Placement = pos=(0,-5,0) rot=(0,0,1;0rad)
  shape: bbox 3.3 x 0.5 x 0.975 mm, 28 faces (baked)
FEATURE [Part::Feature] Part__Feature113  label="Leg043"
  Placement = pos=(0,-9,0) rot=(0,0,1;0rad)
  shape: bbox 3.3 x 0.5 x 0.975 mm, 28 faces (baked)
FEATURE [Part::Feature] Part__Feature114  label="Leg044"
  Placement = pos=(0,-6,0) rot=(0,0,1;0rad)
  shape: bbox 3.3 x 0.5 x 0.975 mm, 28 faces (baked)
FEATURE [Part::Feature] Part__Feature115  label="Leg045"
  Placement = pos=(0,-8,0) rot=(0,0,1;0rad)
  shape: bbox 3.3 x 0.5 x 0.975 mm, 28 faces (baked)
FEATURE [Part::Feature] Part__Feature116  label="Leg046"
  Placement = pos=(0,-4,0) rot=(0,0,1;0rad)
  shape: bbox 3.3 x 0.5 x 0.975 mm, 28 faces (baked)
FEATURE [App::Part] Legs005
  Group = -> [Part__Feature111,Part__Feature110,Part__Feature109,Part__Feature108,Part__Feature116,Part__Feature112,Part__Feature114,Part__Feature106,Part__Feature115,Part__Feature113]
  Origin = -> Origin018
FEATURE [App::Part] GCT_BC075_012  label="GCT_BC075_010-003"
  Group = -> [Part__Feature107,Legs005]
  Origin = -> Origin019
  Placement = pos=(29.7,2,-1.6) rot=(0.707107,0.707107,0;3.14159rad)
FEATURE [Part::Feature] Part__Feature117  label="Leg047"
  Placement = pos=(0,-7,0) rot=(0,0,1;0rad)
  shape: bbox 3.3 x 0.5 x 0.975 mm, 28 faces (baked)
FEATURE [Part::Feature] Part__Feature118  label="Chamfer011"
  Placement = pos=(-3,-4.75,0.475) rot=(0,0,1;0rad)
  shape: bbox 2.1 x 10.75 x 1.5 mm, 86 faces (baked)
FEATURE [Part::Feature] Part__Feature119  label="Leg048"
  Placement = pos=(0,-3,0) rot=(0,0,1;0rad)
  shape: bbox 3.3 x 0.5 x 0.975 mm, 28 faces (baked)
FEATURE [Part::Feature] Part__Feature120  label="Leg049"
  Placement = pos=(0,-2,0) rot=(0,0,1;0rad)
  shape: bbox 3.3 x 0.5 x 0.975 mm, 28 faces (baked)
FEATURE [Part::Feature] Part__Feature121  label="Leg050"
  Placement = pos=(0,-1,0) rot=(0,0,1;0rad)
  shape: bbox 3.3 x 0.5 x 0.975 mm, 28 faces (baked)
FEATURE [Part::Feature] Part__Feature122  label="Leg051"
  shape: bbox 3.3 x 0.5 x 0.975 mm, 28 faces (baked)
FEATURE [Part::Feature] Part__Feature123  label="Leg052"
  Placement = pos=(0,-5,0) rot=(0,0,1;0rad)
  shape: bbox 3.3 x 0.5 x 0.975 mm, 28 faces (baked)
FEATURE [Part::Feature] Part__Feature124  label="Leg053"
  Placement = pos=(0,-9,0) rot=(0,0,1;0rad)
  shape: bbox 3.3 x 0.5 x 0.975 mm, 28 faces (baked)
FEATURE [Part::Feature] Part__Feature125  label="Leg054"
  Placement = pos=(0,-6,0) rot=(0,0,1;0rad)
  shape: bbox 3.3 x 0.5 x 0.975 mm, 28 faces (baked)
FEATURE [Part::Feature] Part__Feature126  label="Leg055"
  Placement = pos=(0,-8,0) rot=(0,0,1;0rad)
  shape: bbox 3.3 x 0.5 x 0.975 mm, 28 faces (baked)
FEATURE [Part::Feature] Part__Feature127  label="Leg056"
  Placement = pos=(0,-4,0) rot=(0,0,1;0rad)
  shape: bbox 3.3 x 0.5 x 0.975 mm, 28 faces (baked)
FEATURE [App::Part] Legs006
  Group = -> [Part__Feature122,Part__Feature121,Part__Feature120,Part__Feature119,Part__Feature127,Part__Feature123,Part__Feature125,Part__Feature117,Part__Feature126,Part__Feature124]
  Origin = -> Origin020
FEATURE [App::Part] GCT_BC075_013  label="GCT_BC075_010-004"
  Group = -> [Part__Feature118,Legs006]
  Origin = -> Origin021
  Placement = pos=(50.5,2,-1.6) rot=(0.707107,0.707107,0;3.14159rad)
FEATURE [App::Link] C6_C_0603_1608Metric_e4ffc2d5bdca_ln_015  label="C16_C_0603_1608Metric_4bdb616e9b067"
  LinkPlacement = pos=(46.1,2.5,0) rot=(0,0,1;1.5708rad)
  LinkedObject = -> Shape011
  Placement = pos=(46.1,2.5,0) rot=(0,0,1;1.5708rad)
FEATURE [Part::Feature] Shape011  label="C6_C_0603_1608Metric_e4ffc2d5bdca001"
  Placement = pos=(45.7,7.5,0) rot=(0,0,1;1.5708rad)
  shape: bbox 0.8 x 1.6 x 0.8 mm, 28 faces (baked)
FEATURE [App::Part] Top_a649
  Group = -> [Shape,Shape001,R82_R_0603_1608Metric_d4caecac030a_ln_,Unnamed,C6_C_0603_1608Metric_e4ffc2d5bdca_ln_001,Shape002,R82_R_0603_1608Metric_d4caecac030a_ln_001,R82_R_0603_1608Metric_d4caecac030a_ln_002,C6_C_0603_1608Metric_e4ffc2d5bdca_ln_002,R82_R_0603_1608Metric_d4caecac030a_ln_003,C6_C_0603_1608Metric_e4ffc2d5bdca_ln_003,DIL_64,C6_C_0603_1608Metric_e4ffc2d5bdca_ln_,Unnamed001,GCT_BC075_06,+6 more]
  Origin = -> Origin003
FEATURE [App::Part] Step_Models_a649
  Group = -> [Top_a649,Bot_a649]
  Origin = -> Origin002
FEATURE [App::Part] Board_a649  label="Ultra-VDP"
  Group = -> [Board_Geoms_a649,Step_Models_a649]
  Origin = -> Origin001
